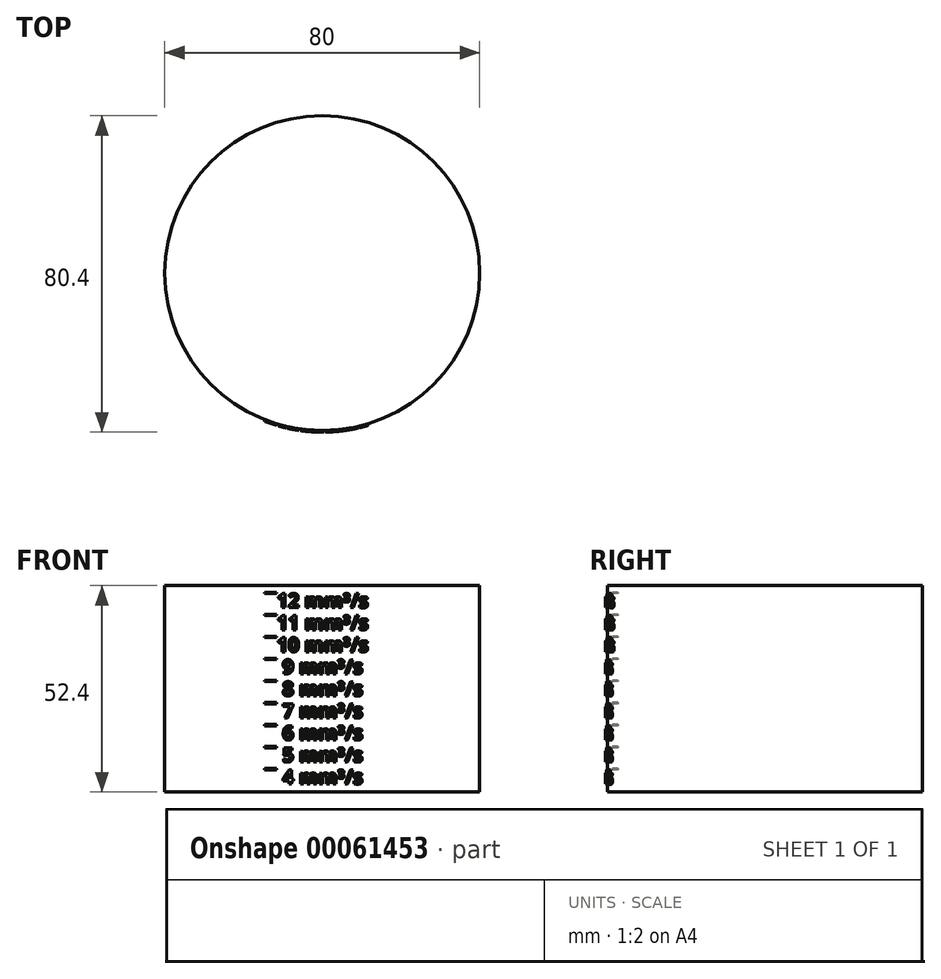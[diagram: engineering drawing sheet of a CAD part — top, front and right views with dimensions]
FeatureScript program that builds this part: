
annotation { "Feature Type Name" : "Feature", "Feature Type Description" : "" }
export const myFeature = defineFeature(function(context is Context, id is Id, definition is map)
    precondition{}
    {
        {
            var Q0;
            Q0=qCreatedBy(makeId("Top.planeOp"),FACE);
            var sketch = newSketch(context, id + "F0", { "sketchPlane" : qUnion([Q0])});
            skCircle(sketch, "E0", {"center": v(0, 0) * mm, "radius": 40 * mm});
            skSolve(sketch);
        }
        {
            var Q0;
            Q0=makeQuery(id+"F0.imprint","IMPRINT",FACE,{"disambiguationData":[TD([[makeQuery(id+"F0.imprint","IMPRINT",EDGE,{"derivedFrom":sQuery(id+"F0.wireOp",EDGE,"E0")}),1.0]])]});
            extrude(context, id + "F1", {"entities" : qUnion([Q0]), "depth" : ((5.6 * 9) + 2) * mm});
        }
        {
            var Q0;
            Q0=qCreatedBy(makeId("Front.planeOp"),FACE);
            cPlane(context, id + "F2", {"entities" : qUnion([Q0]), "cplaneType" : CPlaneType.OFFSET, "offset" : 80 * mm, "width" : 150 * mm, "height" : 150 * mm});
        }
        {
            var Q0;
            Q0=qCreatedBy(id+"F2.planeOp",FACE);
            var sketch = newSketch(context, id + "F3", { "sketchPlane" : qUnion([Q0])});
            skText(sketch, "E1", { "text": "4 mm³/s", "fontName": "OpenSans-Bold.ttf"});
            skText(sketch, "E2", { "text": "9 mm³/s", "fontName": "OpenSans-Bold.ttf"});
            skText(sketch, "E3", { "text": "8 mm³/s", "fontName": "OpenSans-Bold.ttf"});
            skText(sketch, "E4", { "text": "7 mm³/s", "fontName": "OpenSans-Bold.ttf"});
            skText(sketch, "E5", { "text": "6 mm³/s", "fontName": "OpenSans-Bold.ttf"});
            skText(sketch, "E6", { "text": "11 mm³/s", "fontName": "OpenSans-Bold.ttf"});
            skText(sketch, "E7", { "text": "10 mm³/s", "fontName": "OpenSans-Bold.ttf"});
            skText(sketch, "E8", { "text": "5 mm³/s", "fontName": "OpenSans-Bold.ttf"});
            skLineSegment(sketch, "E9.bottom", {"start": v(-11.61, 5.6) * mm, "end": v(-14.61, 5.6) * mm});
            skLineSegment(sketch, "E9.top", {"start": v(-11.61, 5.9) * mm, "end": v(-14.61, 5.9) * mm});
            skLineSegment(sketch, "E9.left", {"start": v(-11.61, 5.6) * mm, "end": v(-11.61, 5.9) * mm});
            skLineSegment(sketch, "E9.right", {"start": v(-14.61, 5.6) * mm, "end": v(-14.61, 5.9) * mm});
            skLineSegment(sketch, "E10.0.1.0", {"start": v(-11.61, 11.2) * mm, "end": v(-14.61, 11.2) * mm});
            skLineSegment(sketch, "E10.0.1.1", {"start": v(-11.61, 11.5) * mm, "end": v(-14.61, 11.5) * mm});
            skLineSegment(sketch, "E10.0.1.2", {"start": v(-14.61, 11.2) * mm, "end": v(-14.61, 11.5) * mm});
            skLineSegment(sketch, "E10.0.1.3", {"start": v(-11.61, 11.2) * mm, "end": v(-11.61, 11.5) * mm});
            skLineSegment(sketch, "E10.0.2.0", {"start": v(-11.61, 16.8) * mm, "end": v(-14.61, 16.8) * mm});
            skLineSegment(sketch, "E10.0.2.1", {"start": v(-11.61, 17.1) * mm, "end": v(-14.61, 17.1) * mm});
            skLineSegment(sketch, "E10.0.2.2", {"start": v(-14.61, 16.8) * mm, "end": v(-14.61, 17.1) * mm});
            skLineSegment(sketch, "E10.0.2.3", {"start": v(-11.61, 16.8) * mm, "end": v(-11.61, 17.1) * mm});
            skLineSegment(sketch, "E10.0.3.0", {"start": v(-11.61, 22.4) * mm, "end": v(-14.61, 22.4) * mm});
            skLineSegment(sketch, "E10.0.3.1", {"start": v(-11.61, 22.7) * mm, "end": v(-14.61, 22.7) * mm});
            skLineSegment(sketch, "E10.0.3.2", {"start": v(-14.61, 22.4) * mm, "end": v(-14.61, 22.7) * mm});
            skLineSegment(sketch, "E10.0.3.3", {"start": v(-11.61, 22.4) * mm, "end": v(-11.61, 22.7) * mm});
            skLineSegment(sketch, "E10.0.4.0", {"start": v(-11.61, 28) * mm, "end": v(-14.61, 28) * mm});
            skLineSegment(sketch, "E10.0.4.1", {"start": v(-11.61, 28.3) * mm, "end": v(-14.61, 28.3) * mm});
            skLineSegment(sketch, "E10.0.4.2", {"start": v(-14.61, 28) * mm, "end": v(-14.61, 28.3) * mm});
            skLineSegment(sketch, "E10.0.4.3", {"start": v(-11.61, 28) * mm, "end": v(-11.61, 28.3) * mm});
            skLineSegment(sketch, "E10.0.5.0", {"start": v(-11.61, 33.6) * mm, "end": v(-14.61, 33.6) * mm});
            skLineSegment(sketch, "E10.0.5.1", {"start": v(-11.61, 33.9) * mm, "end": v(-14.61, 33.9) * mm});
            skLineSegment(sketch, "E10.0.5.2", {"start": v(-14.61, 33.6) * mm, "end": v(-14.61, 33.9) * mm});
            skLineSegment(sketch, "E10.0.5.3", {"start": v(-11.61, 33.6) * mm, "end": v(-11.61, 33.9) * mm});
            skLineSegment(sketch, "E10.0.6.0", {"start": v(-11.61, 39.2) * mm, "end": v(-14.61, 39.2) * mm});
            skLineSegment(sketch, "E10.0.6.1", {"start": v(-11.61, 39.5) * mm, "end": v(-14.61, 39.5) * mm});
            skLineSegment(sketch, "E10.0.6.2", {"start": v(-14.61, 39.2) * mm, "end": v(-14.61, 39.5) * mm});
            skLineSegment(sketch, "E10.0.6.3", {"start": v(-11.61, 39.2) * mm, "end": v(-11.61, 39.5) * mm});
            skLineSegment(sketch, "E10.0.7.0", {"start": v(-11.61, 44.8) * mm, "end": v(-14.61, 44.8) * mm});
            skLineSegment(sketch, "E10.0.7.1", {"start": v(-11.61, 45.1) * mm, "end": v(-14.61, 45.1) * mm});
            skLineSegment(sketch, "E10.0.7.2", {"start": v(-14.61, 44.8) * mm, "end": v(-14.61, 45.1) * mm});
            skLineSegment(sketch, "E10.0.7.3", {"start": v(-11.61, 44.8) * mm, "end": v(-11.61, 45.1) * mm});
            skLineSegment(sketch, "E10.direction1", {"start": v(-14.61, 5.6) * mm, "end": v(18.86, 5.6) * mm, "construction": true});
            skLineSegment(sketch, "E10.direction2", {"start": v(-14.61, 5.6) * mm, "end": v(-14.61, 11.2) * mm, "construction": true});
            skText(sketch, "E11", { "text": "12 mm³/s", "fontName": "OpenSans-Bold.ttf"});
            skLineSegment(sketch, "E12.0.7.3", {"start": v(15.04, 45.63) * mm, "end": v(15.04, 45.93) * mm});
            skLineSegment(sketch, "E13.0.0.8", {"start": v(-11.61, 50.4) * mm, "end": v(-14.61, 50.4) * mm});
            skLineSegment(sketch, "E13.3.0.8", {"start": v(-11.61, 50.7) * mm, "end": v(-14.61, 50.7) * mm});
            skLineSegment(sketch, "E13.6.0.8", {"start": v(-14.61, 50.4) * mm, "end": v(-14.61, 50.7) * mm});
            skLineSegment(sketch, "E13.9.0.8", {"start": v(-11.61, 50.4) * mm, "end": v(-11.61, 50.7) * mm});
            const initialGuessF3  = {"E1": [-0.01011, 0.002, 1, 0, 0.0036], "E2": [-0.01011, 0.03, 1, 0, 0.0036], "E3": [-0.01011, 0.0244, 1, 0, 0.0036], "E4": [-0.01011, 0.0188, 1, 0, 0.0036], "E5": [-0.01011, 0.0132, 1, 0, 0.0036], "E6": [-0.01154, 0.0412, 1, 0, 0.0036], "E7": [-0.01154, 0.0356, 1, 0, 0.0036], "E8": [-0.01011, 0.0076, 1, 0, 0.0036], "E11": [-0.01154, 0.0468, 1, 0, 0.0036]};
            skSetInitialGuess(sketch, initialGuessF3);
            skSolve(sketch);
        }
        {
            var Q0;
            Q0 = qSketchRegion(id + "F3", true);
            extrude(context, id + "F4", {"entities" : qUnion([Q0]), "operationType" : NewBodyOperationType.ADD, "endBound" : BoundingType.UP_TO_NEXT, "oppositeDirection" : true, "depth" : 25 * mm});
        }
        {
            var Q0;
            Q0=makeQuery(id+"F1.opExtrude","CAP_FACE",FACE,{"disambiguationData":[OSD([sQuery(id+"F0.wireOp",EDGE,"E0")])],"isStart":false});
            var sketch = newSketch(context, id + "F5", { "sketchPlane" : qUnion([Q0])});
            skCircle(sketch, "E14.0", {"center": v(0, 0) * mm, "radius": 40 * mm});
            skCircle(sketch, "E15.0", {"center": v(0, 0) * mm, "radius": 40.4 * mm});
            skCircle(sketch, "E16.0", {"center": v(0, 0) * mm, "radius": 90.4 * mm});
            skSolve(sketch);
        }
        {
            var Q0;
            Q0=makeQuery(id+"F5.imprint","IMPRINT",FACE,{"disambiguationData":[TD([[makeQuery(id+"F5.imprint","IMPRINT",EDGE,{"derivedFrom":sQuery(id+"F5.wireOp",EDGE,"E15.0")}),-1.0]])]});
            extrude(context, id + "F6", {"entities" : qUnion([Q0]), "operationType" : NewBodyOperationType.REMOVE, "endBound" : BoundingType.THROUGH_ALL, "oppositeDirection" : true, "depth" : 25 * mm});
        }
    });
